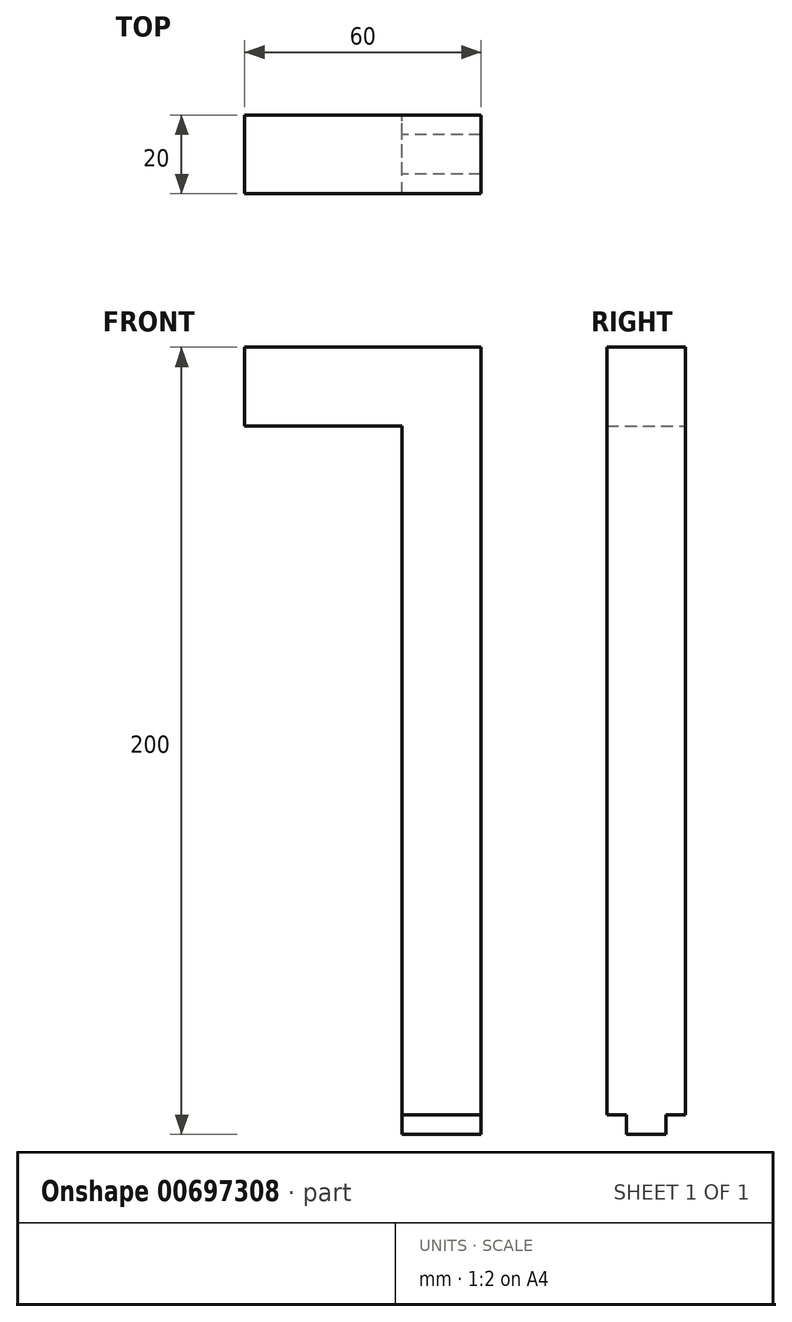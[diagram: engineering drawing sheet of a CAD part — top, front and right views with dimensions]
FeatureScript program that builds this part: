
annotation { "Feature Type Name" : "Feature", "Feature Type Description" : "" }
export const myFeature = defineFeature(function(context is Context, id is Id, definition is map)
    precondition{}
    {
        {
            var Q0;
            Q0=qCreatedBy(makeId("Right.planeOp"),FACE);
            var sketch = newSketch(context, id + "F0", { "sketchPlane" : qUnion([Q0])});
            skLineSegment(sketch, "E0.bottom", {"start": v(-10, -97.5) * mm, "end": v(10, -97.5) * mm});
            skLineSegment(sketch, "E0.top", {"start": v(-10, 97.5) * mm, "end": v(10, 97.5) * mm});
            skLineSegment(sketch, "E0.left", {"start": v(-10, -97.5) * mm, "end": v(-10, 97.5) * mm});
            skLineSegment(sketch, "E0.right", {"start": v(10, -97.5) * mm, "end": v(10, 97.5) * mm});
            skPoint(sketch, "E0.middle", {"position": v(0, 0) * mm});
            skSolve(sketch);
        }
        {
            var Q0;
            Q0=makeQuery(id+"F0.imprint","IMPRINT",FACE,{"disambiguationData":[TD([[makeQuery(id+"F0.imprint","IMPRINT",EDGE,{"derivedFrom":sQuery(id+"F0.wireOp",EDGE,"E0.bottom")}),1.0]])]});
            extrude(context, id + "F1", {"entities" : qUnion([Q0]), "depth" : 20 * mm, "offsetDistance" : 25 * mm});
        }
        {
            var Q0;
            Q0=makeQuery(id+"F1.opExtrude","SWEPT_FACE",FACE,{"disambiguationData":[OSD([sQuery(id+"F0.wireOp",EDGE,"E0.bottom")])]});
            var sketch = newSketch(context, id + "F2", { "sketchPlane" : qUnion([Q0])});
            skLineSegment(sketch, "E1.bottom", {"start": v(20, -5) * mm, "end": v(0, -5) * mm});
            skLineSegment(sketch, "E1.top", {"start": v(20, 5) * mm, "end": v(0, 5) * mm});
            skLineSegment(sketch, "E1.left", {"start": v(20, -5) * mm, "end": v(20, 5) * mm});
            skLineSegment(sketch, "E1.right", {"start": v(0, -5) * mm, "end": v(0, 5) * mm});
            skPoint(sketch, "E1.middle", {"position": v(10, 0) * mm});
            skPoint(sketch, "E1.middle.positionSnap0", {"position": v(10, 10) * mm});
            skPoint(sketch, "E1.centerSnap0", {"position": v(10, 10) * mm});
            skSolve(sketch);
        }
        {
            var Q0;
            Q0=makeQuery(id+"F2.imprint","IMPRINT",FACE,{"disambiguationData":[TD([[makeQuery(id+"F2.imprint","IMPRINT",EDGE,{"derivedFrom":sQuery(id+"F2.wireOp",EDGE,"E1.bottom")}),-1.0]])]});
            extrude(context, id + "F3", {"entities" : qUnion([Q0]), "operationType" : NewBodyOperationType.ADD, "depth" : 5 * mm, "offsetDistance" : 25 * mm});
        }
        {
            var Q0;
            Q0=makeQuery(id+"F3.boolean.opBoolean","MERGE",FACE,{"derivedFrom":[makeQuery(id+"F1.opExtrude","CAP_FACE",FACE,{"disambiguationData":[OSD([sQuery(id+"F0.wireOp",EDGE,"E0.bottom"),sQuery(id+"F0.wireOp",EDGE,"E0.top"),sQuery(id+"F0.wireOp",EDGE,"E0.left"),sQuery(id+"F0.wireOp",EDGE,"E0.right")])],"isStart":true}),makeQuery(id+"F3.opExtrude","SWEPT_FACE",FACE,{"disambiguationData":[OSD([sQuery(id+"F2.wireOp",EDGE,"E1.right")])]})]});
            var sketch = newSketch(context, id + "F4", { "sketchPlane" : qUnion([Q0])});
            skLineSegment(sketch, "E2.bottom", {"start": v(10, 77.5) * mm, "end": v(-10, 77.5) * mm});
            skLineSegment(sketch, "E2.top", {"start": v(10, 97.5) * mm, "end": v(-10, 97.5) * mm});
            skLineSegment(sketch, "E2.left", {"start": v(10, 77.5) * mm, "end": v(10, 97.5) * mm});
            skLineSegment(sketch, "E2.right", {"start": v(-10, 77.5) * mm, "end": v(-10, 97.5) * mm});
            skPoint(sketch, "E2.middle", {"position": v(0, 87.5) * mm});
            skPoint(sketch, "E2.middle.positionSnap0", {"position": v(0, 97.5) * mm});
            skPoint(sketch, "E2.centerSnap0", {"position": v(0, 97.5) * mm});
            skSolve(sketch);
        }
        {
            var Q0;
            Q0=makeQuery(id+"F4.imprint","IMPRINT",FACE,{"disambiguationData":[TD([[makeQuery(id+"F4.imprint","IMPRINT",EDGE,{"derivedFrom":sQuery(id+"F4.wireOp",EDGE,"E2.bottom")}),-1.0]])]});
            extrude(context, id + "F5", {"entities" : qUnion([Q0]), "operationType" : NewBodyOperationType.ADD, "depth" : 40 * mm, "offsetDistance" : 25 * mm});
        }
    });
